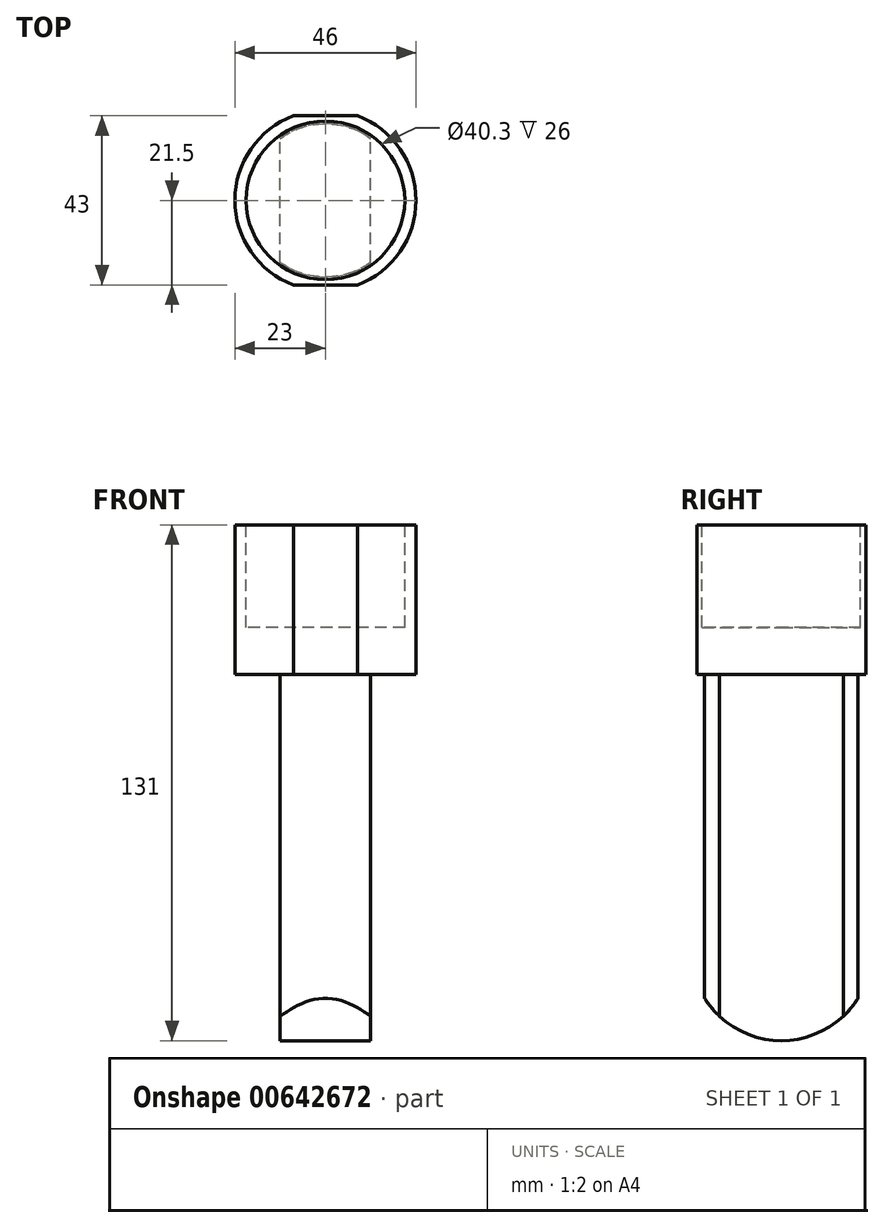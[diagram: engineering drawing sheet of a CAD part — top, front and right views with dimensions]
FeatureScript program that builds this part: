
annotation { "Feature Type Name" : "Feature", "Feature Type Description" : "" }
export const myFeature = defineFeature(function(context is Context, id is Id, definition is map)
    precondition{}
    {
        {
            var Q0;
            Q0=qCreatedBy(makeId("Top.planeOp"),FACE);
            var sketch = newSketch(context, id + "F0", { "sketchPlane" : qUnion([Q0])});
            skArc(sketch, "E0", {"start": v(8.17, -21.5) * mm, "mid": v(23, 0) * mm, "end": v(8.17, 21.5) * mm});
            skLineSegment(sketch, "E1", {"start": v(-8.17, -21.5) * mm, "end": v(8.17, -21.5) * mm});
            skLineSegment(sketch, "E2.MirrorCS", {"start": v(-8.17, 21.5) * mm, "end": v(8.17, 21.5) * mm});
            skArc(sketch, "E3.trimOffspring", {"start": v(-8.17, 21.5) * mm, "mid": v(-23, 0) * mm, "end": v(-8.17, -21.5) * mm});
            skSolve(sketch);
        }
        {
            var Q0;
            Q0=makeQuery(id+"F0.imprint","IMPRINT",FACE,{"disambiguationData":[TD([[makeQuery(id+"F0.imprint","IMPRINT",EDGE,{"derivedFrom":sQuery(id+"F0.wireOp",EDGE,"E0")}),1.0]])]});
            extrude(context, id + "F1", {"entities" : qUnion([Q0]), "depth" : 38 * mm, "offsetDistance" : 25 * mm});
        }
        {
            var Q0;
            Q0=makeQuery(id+"F1.opExtrude","CAP_FACE",FACE,{"disambiguationData":[OSD([sQuery(id+"F0.wireOp",EDGE,"E0"),sQuery(id+"F0.wireOp",EDGE,"E1"),sQuery(id+"F0.wireOp",EDGE,"E2.MirrorCS"),sQuery(id+"F0.wireOp",EDGE,"E3.trimOffspring")])],"isStart":false});
            var sketch = newSketch(context, id + "F2", { "sketchPlane" : qUnion([Q0])});
            skCircle(sketch, "E4", {"center": v(0, 0) * mm, "radius": 20.15 * mm});
            skSolve(sketch);
        }
        {
            var Q0;
            Q0=makeQuery(id+"F2.imprint","IMPRINT",FACE,{"disambiguationData":[TD([[makeQuery(id+"F2.imprint","IMPRINT",EDGE,{"derivedFrom":sQuery(id+"F2.wireOp",EDGE,"E4")}),1.0]])]});
            extrude(context, id + "F3", {"entities" : qUnion([Q0]), "operationType" : NewBodyOperationType.REMOVE, "oppositeDirection" : true, "depth" : 26 * mm, "offsetDistance" : 25 * mm});
        }
        {
            var Q0;
            Q0=makeQuery(id+"F1.opExtrude","CAP_FACE",FACE,{"disambiguationData":[OSD([sQuery(id+"F0.wireOp",EDGE,"E0"),sQuery(id+"F0.wireOp",EDGE,"E1"),sQuery(id+"F0.wireOp",EDGE,"E2.MirrorCS"),sQuery(id+"F0.wireOp",EDGE,"E3.trimOffspring")])],"isStart":true});
            var sketch = newSketch(context, id + "F4", { "sketchPlane" : qUnion([Q0])});
            skArc(sketch, "E5", {"start": v(11.5, 15.75) * mm, "mid": v(0, 19.5) * mm, "end": v(-11.5, 15.75) * mm});
            skLineSegment(sketch, "E6", {"start": v(-11.5, 15.75) * mm, "end": v(-11.5, -15.75) * mm});
            skLineSegment(sketch, "E7.MirrorCS", {"start": v(11.5, 15.75) * mm, "end": v(11.5, -15.75) * mm});
            skArc(sketch, "E8.trimOffspring", {"start": v(-11.5, -15.75) * mm, "mid": v(0, -19.5) * mm, "end": v(11.5, -15.75) * mm});
            skSolve(sketch);
        }
        {
            var Q0;
            Q0=makeQuery(id+"F4.imprint","IMPRINT",FACE,{"disambiguationData":[TD([[makeQuery(id+"F4.imprint","IMPRINT",EDGE,{"derivedFrom":sQuery(id+"F4.wireOp",EDGE,"E5")}),1.0]])]});
            extrude(context, id + "F5", {"entities" : qUnion([Q0]), "operationType" : NewBodyOperationType.ADD, "depth" : 93 * mm, "offsetDistance" : 25 * mm});
        }
        {
            var Q0;
            Q0=makeQuery(id+"F5.opExtrude","SWEPT_FACE",FACE,{"disambiguationData":[OSD([sQuery(id+"F4.wireOp",EDGE,"E7.MirrorCS")])]});
            var sketch = newSketch(context, id + "F6", { "sketchPlane" : qUnion([Q0])});
            skCircle(sketch, "E9", {"center": v(0, -70) * mm, "radius": 23 * mm});
            skLineSegment(sketch, "E10", {"start": v(22.61, -74.2) * mm, "end": v(29.48, -115.45) * mm});
            skLineSegment(sketch, "E11", {"start": v(-32.06, -119.32) * mm, "end": v(29.48, -115.45) * mm});
            skLineSegment(sketch, "E12", {"start": v(29.48, -115.45) * mm, "end": v(-32.06, -119.32) * mm});
            skLineSegment(sketch, "E13", {"start": v(-32.06, -119.32) * mm, "end": v(-21.85, -77.2) * mm});
            skSolve(sketch);
        }
        {
            var Q0;
            {var subQ0=sQuery(id+"F6.wireOp",EDGE,"E10");Q0=makeQuery(id+"F6.imprint","IMPRINT",FACE,{"disambiguationData":[TD([[makeQuery(id+"F6.imprint","IMPRINT",EDGE,{"derivedFrom":subQ0}),-1.0]])]});}
            var Q1;
            {var subQ0=sQuery(id+"F6.wireOp",EDGE,"E9");var subQ1=sQuery(id+"F4.wireOp",EDGE,"E7.MirrorCS");var subQ4=makeQuery(id+"F5.opExtrude","CAP_EDGE",EDGE,{"disambiguationData":[OSD([subQ1])],"isStart":false});var subQ5=makeQuery(id+"F6.imprint","INTERSECT",VERTEX,{"derivedFrom":[subQ4,subQ0]});Q1=makeQuery(id+"F6.imprint","IMPRINT",FACE,{"disambiguationData":[TD([[makeQuery(id+"F6.imprint","IMPRINT",EDGE,{"disambiguationData":[TD([[subQ5,1.0]])],"derivedFrom":subQ0}),-1.0]])]});}
            var Q2;
            {var subQ0=sQuery(id+"F6.wireOp",EDGE,"E9");var subQ1=sQuery(id+"F4.wireOp",EDGE,"E7.MirrorCS");var subQ2=makeQuery(id+"F5.opExtrude","CAP_EDGE",EDGE,{"disambiguationData":[OSD([subQ1])],"isStart":false});var subQ3=makeQuery(id+"F6.imprint","INTERSECT",VERTEX,{"derivedFrom":[subQ2,subQ0]});Q2=makeQuery(id+"F6.imprint","IMPRINT",FACE,{"disambiguationData":[TD([[makeQuery(id+"F6.imprint","IMPRINT",EDGE,{"disambiguationData":[TD([[subQ3,-1.0]])],"derivedFrom":subQ0}),-1.0]])]});}
            extrude(context, id + "F7", {"entities" : qUnion([Q0, Q1, Q2]), "operationType" : NewBodyOperationType.REMOVE, "endBound" : BoundingType.THROUGH_ALL, "oppositeDirection" : true, "depth" : 25 * mm, "offsetDistance" : 25 * mm});
        }
    });
